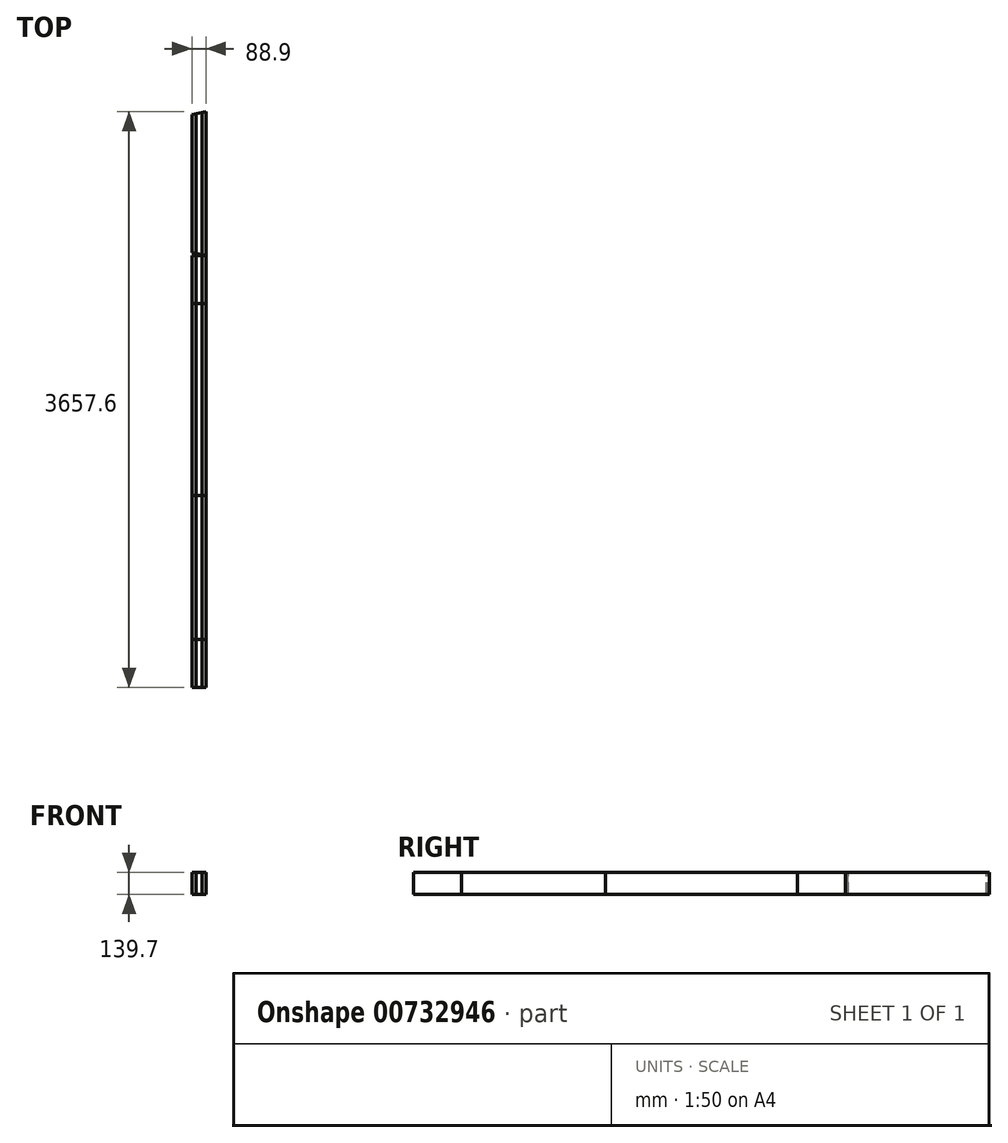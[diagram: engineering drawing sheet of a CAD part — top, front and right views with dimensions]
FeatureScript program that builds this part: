
annotation { "Feature Type Name" : "Feature", "Feature Type Description" : "" }
export const myFeature = defineFeature(function(context is Context, id is Id, definition is map)
    precondition{}
    {
        {
            var Q0;
            Q0=qCreatedBy(makeId("Front.planeOp"),FACE);
            var sketch = newSketch(context, id + "F0", { "sketchPlane" : qUnion([Q0])});
            skLineSegment(sketch, "E0.bottom", {"start": v(44.45, 69.85) * mm, "end": v(-44.45, 69.85) * mm});
            skLineSegment(sketch, "E0.top", {"start": v(44.45, -69.85) * mm, "end": v(-44.45, -69.85) * mm});
            skLineSegment(sketch, "E0.left", {"start": v(44.45, 69.85) * mm, "end": v(44.45, -69.85) * mm});
            skLineSegment(sketch, "E0.right", {"start": v(-44.45, 69.85) * mm, "end": v(-44.45, -69.85) * mm});
            skPoint(sketch, "E0.middle", {"position": v(0, 0) * mm});
            skSolve(sketch);
        }
        {
            var Q0;
            Q0=qCreatedBy(makeId("Front.planeOp"),FACE);
            var sketch = newSketch(context, id + "F1", { "sketchPlane" : qUnion([Q0])});
            skLineSegment(sketch, "E1.bottom", {"start": v(19.05, 69.85) * mm, "end": v(-19.05, 69.85) * mm});
            skLineSegment(sketch, "E1.top", {"start": v(19.05, -69.85) * mm, "end": v(-19.05, -69.85) * mm});
            skLineSegment(sketch, "E1.left", {"start": v(19.05, 69.85) * mm, "end": v(19.05, -69.85) * mm});
            skLineSegment(sketch, "E1.right", {"start": v(-19.05, 69.85) * mm, "end": v(-19.05, -69.85) * mm});
            skPoint(sketch, "E1.middle", {"position": v(0, 0) * mm});
            skSolve(sketch);
        }
        {
            var Q0;
            Q0 = qSketchRegion(id + "F0", true);
            extrude(context, id + "F2", {"entities" : qUnion([Q0]), "depth" : 1219.2 * mm, "offsetDistance" : 25.4 * mm});
        }
        {
            var Q0;
            Q0 = qSketchRegion(id + "F0", true);
            extrude(context, id + "F3", {"entities" : qUnion([Q0]), "depth" : 2438.4 * mm, "offsetDistance" : 25.4 * mm});
        }
        {
            var Q0;
            Q0 = qSketchRegion(id + "F0", true);
            extrude(context, id + "F4", {"entities" : qUnion([Q0]), "depth" : 3352.8 * mm, "offsetDistance" : 25.4 * mm});
        }
        {
            var Q0;
            Q0 = qSketchRegion(id + "F0", true);
            extrude(context, id + "F5", {"entities" : qUnion([Q0]), "depth" : 3657.6 * mm, "offsetDistance" : 25.4 * mm});
        }
        {
            var Q0;
            Q0 = qSketchRegion(id + "F1", true);
            extrude(context, id + "F6", {"entities" : qUnion([Q0]), "depth" : 2438.4 * mm, "offsetDistance" : 25.4 * mm});
        }
        {
            var Q0;
            Q0 = qSketchRegion(id + "F1", true);
            extrude(context, id + "F7", {"entities" : qUnion([Q0]), "depth" : 3657.6 * mm, "offsetDistance" : 25.4 * mm});
        }
        {
            var Q0;
            Q0 = qSketchRegion(id + "F0", true);
            extrude(context, id + "F8", {"entities" : qUnion([Q0]), "depth" : 914.4 * mm, "offsetDistance" : 25.4 * mm});
        }
        {
            var Q0;
            Q0=makeQuery(id+"F8.opExtrude","SWEPT_FACE",FACE,{"disambiguationData":[OSD([sQuery(id+"F0.wireOp",EDGE,"E0.bottom")])]});
            var sketch = newSketch(context, id + "F9", { "sketchPlane" : qUnion([Q0])});
            skLineSegment(sketch, "E2", {"start": v(44.45, 0) * mm, "end": v(-44.45, -18.9) * mm});
            skLineSegment(sketch, "E3", {"start": v(-44.45, -18.9) * mm, "end": v(-44.45, 0) * mm});
            skLineSegment(sketch, "E4", {"start": v(-44.45, 0) * mm, "end": v(44.45, 0) * mm});
            skLineSegment(sketch, "E5", {"start": v(-44.45, -914.4) * mm, "end": v(-44.45, -895.5) * mm});
            skLineSegment(sketch, "E6", {"start": v(-44.45, -895.5) * mm, "end": v(44.45, -914.4) * mm});
            skLineSegment(sketch, "E7", {"start": v(44.45, -914.4) * mm, "end": v(-44.45, -914.4) * mm});
            skSolve(sketch);
        }
        {
            var Q0;
            Q0 = qSketchRegion(id + "F9", true);
            extrude(context, id + "F10", {"entities" : qUnion([Q0]), "operationType" : NewBodyOperationType.REMOVE, "endBound" : BoundingType.THROUGH_ALL, "oppositeDirection" : true, "depth" : 25.4 * mm, "offsetDistance" : 25.4 * mm});
        }
    });
